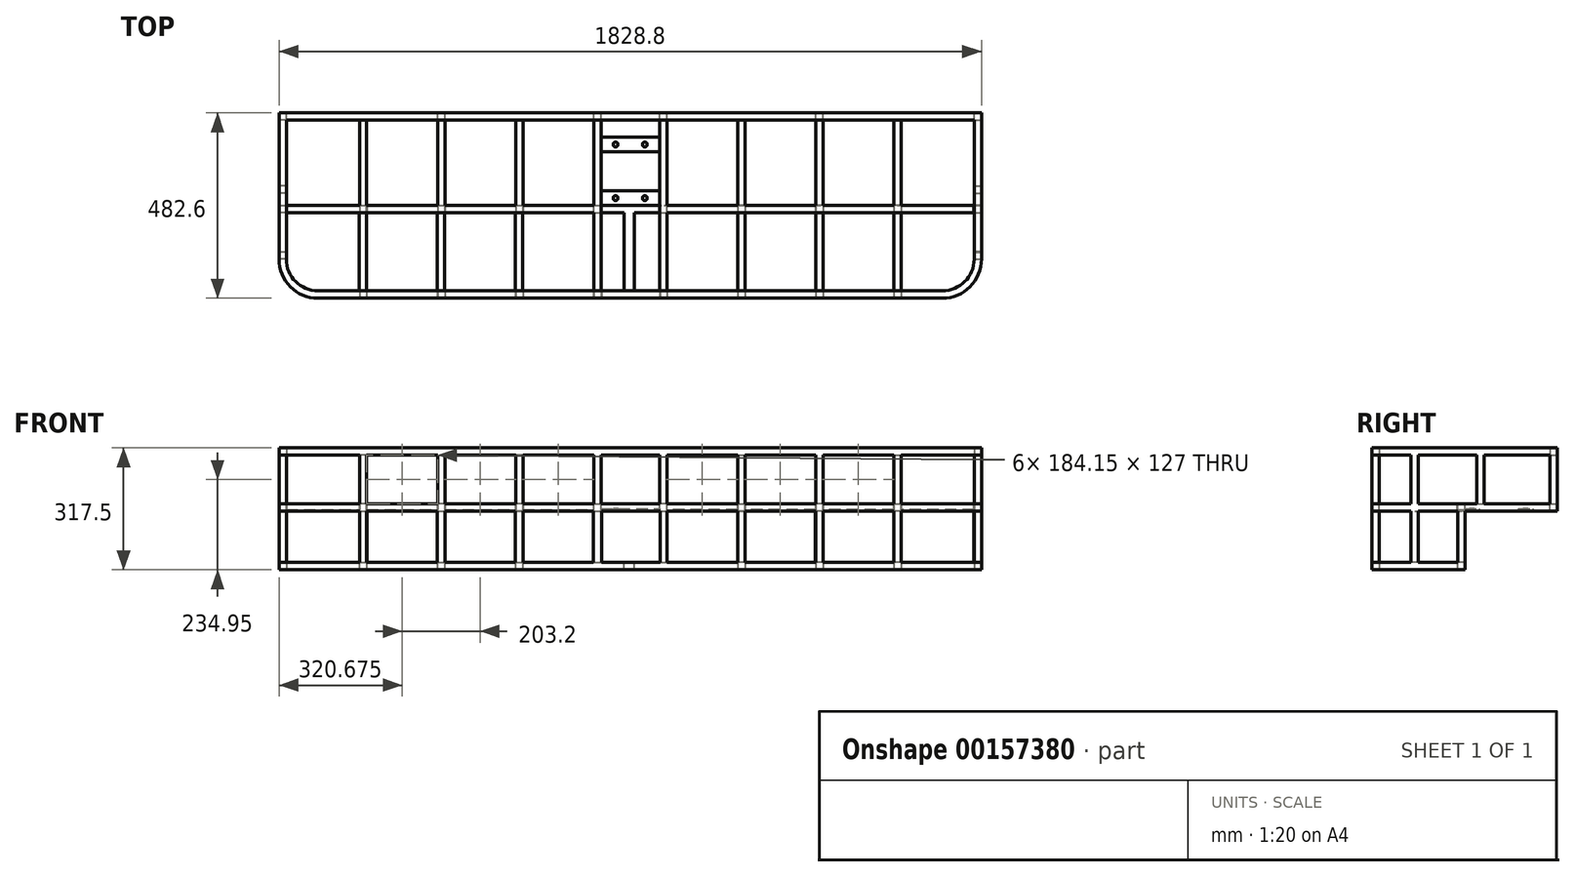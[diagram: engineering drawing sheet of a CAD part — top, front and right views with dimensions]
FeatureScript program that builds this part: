
annotation { "Feature Type Name" : "Feature", "Feature Type Description" : "" }
export const myFeature = defineFeature(function(context is Context, id is Id, definition is map)
    precondition{}
    {
        {
            var Q0;
            Q0=qCreatedBy(makeId("Top.planeOp"),FACE);
            var sketch = newSketch(context, id + "F0", { "sketchPlane" : qUnion([Q0])});
            skLineSegment(sketch, "E0", {"start": v(0, 0) * mm, "end": v(0, -133.91) * mm, "construction": true});
            skLineSegment(sketch, "E1", {"start": v(0, 0) * mm, "end": v(-895.35, 0) * mm});
            skLineSegment(sketch, "E2", {"start": v(-914.4, 0) * mm, "end": v(-914.4, -381) * mm});
            skLineSegment(sketch, "E3", {"start": v(-812.8, -482.6) * mm, "end": v(0, -482.6) * mm});
            skPoint(sketch, "E4.visualSharp", {"position": v(-914.4, -482.6) * mm});
            skArc(sketch, "E4.filletArc", {"start": v(-914.4, -381) * mm, "mid": v(-884.64, -452.84) * mm, "end": v(-812.8, -482.6) * mm});
            skLineSegment(sketch, "E5.0", {"start": v(-812.8, -463.55) * mm, "end": v(0, -463.55) * mm});
            skArc(sketch, "E5.1", {"start": v(-895.35, -381) * mm, "mid": v(-871.17, -439.37) * mm, "end": v(-812.8, -463.55) * mm});
            skLineSegment(sketch, "E5.2", {"start": v(-895.35, -19.05) * mm, "end": v(-895.35, -381) * mm});
            skLineSegment(sketch, "E5.3", {"start": v(0, -19.05) * mm, "end": v(-895.35, -19.05) * mm});
            skLineSegment(sketch, "E6", {"start": v(-895.35, -19.05) * mm, "end": v(-895.35, 0) * mm});
            skLineSegment(sketch, "E7", {"start": v(-914.4, 0) * mm, "end": v(-895.35, 0) * mm});
            skLineSegment(sketch, "E8", {"start": v(0, 0) * mm, "end": v(0, -19.05) * mm});
            skLineSegment(sketch, "E9", {"start": v(0, -463.55) * mm, "end": v(0, -482.6) * mm});
            skSolve(sketch);
        }
        {
            var Q0;
            Q0 = qSketchRegion(id + "F0", true);
            extrude(context, id + "F1", {"entities" : qUnion([Q0]), "depth" : 19.05 * mm});
        }
        {
            var Q0;
            Q0=makeQuery(id+"F1.opExtrude","CAP_FACE",FACE,{"disambiguationData":[OSD([sQuery(id+"F0.wireOp",EDGE,"E1"),sQuery(id+"F0.wireOp",EDGE,"E2"),sQuery(id+"F0.wireOp",EDGE,"E3"),sQuery(id+"F0.wireOp",EDGE,"E4.filletArc"),sQuery(id+"F0.wireOp",EDGE,"E5.0"),sQuery(id+"F0.wireOp",EDGE,"E5.1"),sQuery(id+"F0.wireOp",EDGE,"E5.2"),sQuery(id+"F0.wireOp",EDGE,"E5.3"),sQuery(id+"F0.wireOp",EDGE,"E7"),sQuery(id+"F0.wireOp",EDGE,"E8"),sQuery(id+"F0.wireOp",EDGE,"E9")])],"isStart":false});
            cPlane(context, id + "F2", {"entities" : qUnion([Q0]), "cplaneType" : CPlaneType.OFFSET, "offset" : 127 * mm, "width" : 152.4 * mm, "height" : 152.4 * mm});
        }
        {
            var Q0;
            Q0=qCreatedBy(id+"F2.planeOp",FACE);
            var sketch = newSketch(context, id + "F3", { "sketchPlane" : qUnion([Q0])});
            skLineSegment(sketch, "E10.0", {"start": v(-812.8, -482.6) * mm, "end": v(0, -482.6) * mm});
            skLineSegment(sketch, "E10.1", {"start": v(-812.8, -463.55) * mm, "end": v(0, -463.55) * mm});
            skLineSegment(sketch, "E10.2", {"start": v(0, -463.55) * mm, "end": v(0, -482.6) * mm});
            skArc(sketch, "E10.3", {"start": v(-895.35, -381) * mm, "mid": v(-871.17, -439.37) * mm, "end": v(-812.8, -463.55) * mm});
            skArc(sketch, "E10.4", {"start": v(-914.4, -381) * mm, "mid": v(-884.64, -452.84) * mm, "end": v(-812.8, -482.6) * mm});
            skLineSegment(sketch, "E10.5", {"start": v(-914.4, 0) * mm, "end": v(-914.4, -381) * mm});
            skLineSegment(sketch, "E10.6", {"start": v(-895.35, -19.05) * mm, "end": v(-895.35, -381) * mm});
            skLineSegment(sketch, "E10.7", {"start": v(0, 0) * mm, "end": v(-914.4, 0) * mm});
            skLineSegment(sketch, "E10.8", {"start": v(0, -19.05) * mm, "end": v(-895.35, -19.05) * mm});
            skLineSegment(sketch, "E10.9", {"start": v(0, 0) * mm, "end": v(0, -19.05) * mm});
            skSolve(sketch);
        }
        {
            var Q0;
            Q0 = qSketchRegion(id + "F3", true);
            extrude(context, id + "F4", {"entities" : qUnion([Q0]), "depth" : 19.05 * mm});
        }
        {
            var Q0;
            Q0=makeQuery(id+"F1.opExtrude","CAP_FACE",FACE,{"disambiguationData":[OSD([sQuery(id+"F0.wireOp",EDGE,"E1"),sQuery(id+"F0.wireOp",EDGE,"E2"),sQuery(id+"F0.wireOp",EDGE,"E3"),sQuery(id+"F0.wireOp",EDGE,"E4.filletArc"),sQuery(id+"F0.wireOp",EDGE,"E5.0"),sQuery(id+"F0.wireOp",EDGE,"E5.1"),sQuery(id+"F0.wireOp",EDGE,"E5.2"),sQuery(id+"F0.wireOp",EDGE,"E5.3"),sQuery(id+"F0.wireOp",EDGE,"E7"),sQuery(id+"F0.wireOp",EDGE,"E8"),sQuery(id+"F0.wireOp",EDGE,"E9")])],"isStart":true});
            cPlane(context, id + "F5", {"entities" : qUnion([Q0]), "cplaneType" : CPlaneType.OFFSET, "offset" : 152.4 * mm, "width" : 152.4 * mm, "height" : 152.4 * mm});
        }
        {
            var Q0;
            Q0=qCreatedBy(id+"F5.planeOp",FACE);
            var sketch = newSketch(context, id + "F6", { "sketchPlane" : qUnion([Q0])});
            skLineSegment(sketch, "E11.0", {"start": v(-812.8, 482.6) * mm, "end": v(0, 482.6) * mm});
            skLineSegment(sketch, "E11.1", {"start": v(-812.8, 463.55) * mm, "end": v(0, 463.55) * mm});
            skLineSegment(sketch, "E11.2", {"start": v(0, 463.55) * mm, "end": v(0, 482.6) * mm});
            skArc(sketch, "E11.3", {"start": v(-914.4, 381) * mm, "mid": v(-884.64, 452.84) * mm, "end": v(-812.8, 482.6) * mm});
            skArc(sketch, "E11.4", {"start": v(-895.35, 381) * mm, "mid": v(-871.17, 439.37) * mm, "end": v(-812.8, 463.55) * mm});
            skLineSegment(sketch, "E12", {"start": v(-914.4, 381) * mm, "end": v(-914.4, 240.55) * mm});
            skLineSegment(sketch, "E13", {"start": v(-914.4, 240.55) * mm, "end": v(0, 240.55) * mm});
            skLineSegment(sketch, "E14.0", {"start": v(-895.35, 259.6) * mm, "end": v(0, 259.6) * mm});
            skLineSegment(sketch, "E14.1", {"start": v(-895.35, 381) * mm, "end": v(-895.35, 259.6) * mm});
            skLineSegment(sketch, "E15", {"start": v(0, 259.6) * mm, "end": v(0, 240.55) * mm});
            skSolve(sketch);
        }
        {
            var Q0;
            Q0 = qSketchRegion(id + "F6", true);
            extrude(context, id + "F7", {"entities" : qUnion([Q0]), "oppositeDirection" : true, "depth" : 19.05 * mm});
        }
        {
            var Q0;
            Q0=makeQuery(id+"F1.opExtrude","CAP_FACE",FACE,{"disambiguationData":[OSD([sQuery(id+"F0.wireOp",EDGE,"E1"),sQuery(id+"F0.wireOp",EDGE,"E2"),sQuery(id+"F0.wireOp",EDGE,"E3"),sQuery(id+"F0.wireOp",EDGE,"E4.filletArc"),sQuery(id+"F0.wireOp",EDGE,"E5.0"),sQuery(id+"F0.wireOp",EDGE,"E5.1"),sQuery(id+"F0.wireOp",EDGE,"E5.2"),sQuery(id+"F0.wireOp",EDGE,"E5.3"),sQuery(id+"F0.wireOp",EDGE,"E7"),sQuery(id+"F0.wireOp",EDGE,"E8"),sQuery(id+"F0.wireOp",EDGE,"E9")])],"isStart":false});
            var sketch = newSketch(context, id + "F8", { "sketchPlane" : qUnion([Q0])});
            skLineSegment(sketch, "E16.bottom", {"start": v(-76.2, -463.55) * mm, "end": v(-95.25, -463.55) * mm});
            skLineSegment(sketch, "E16.top", {"start": v(-76.2, -19.05) * mm, "end": v(-95.25, -19.05) * mm});
            skLineSegment(sketch, "E16.left", {"start": v(-76.2, -463.55) * mm, "end": v(-76.2, -19.05) * mm});
            skLineSegment(sketch, "E16.right", {"start": v(-95.25, -463.55) * mm, "end": v(-95.25, -19.05) * mm});
            skLineSegment(sketch, "E17.1.0.0", {"start": v(-279.4, -260.58) * mm, "end": v(-279.4, -19.05) * mm});
            skLineSegment(sketch, "E17.1.0.1", {"start": v(-298.45, -260.58) * mm, "end": v(-298.45, -19.05) * mm});
            skLineSegment(sketch, "E17.1.0.3", {"start": v(-279.4, -19.05) * mm, "end": v(-298.45, -19.05) * mm});
            skLineSegment(sketch, "E17.2.0.0", {"start": v(-482.6, -259.76) * mm, "end": v(-482.6, -19.05) * mm});
            skLineSegment(sketch, "E17.2.0.1", {"start": v(-501.65, -259.76) * mm, "end": v(-501.65, -19.05) * mm});
            skLineSegment(sketch, "E17.2.0.3", {"start": v(-482.6, -19.05) * mm, "end": v(-501.65, -19.05) * mm});
            skLineSegment(sketch, "E17.3.0.0", {"start": v(-685.8, -259.76) * mm, "end": v(-685.8, -19.05) * mm});
            skLineSegment(sketch, "E17.3.0.1", {"start": v(-704.85, -259.76) * mm, "end": v(-704.85, -19.05) * mm});
            skLineSegment(sketch, "E17.3.0.3", {"start": v(-685.8, -19.05) * mm, "end": v(-704.85, -19.05) * mm});
            skLineSegment(sketch, "E17.direction1", {"start": v(-95.25, -463.55) * mm, "end": v(-298.45, -463.55) * mm, "construction": true});
            skLineSegment(sketch, "E18", {"start": v(-482.6, -259.76) * mm, "end": v(-501.65, -259.76) * mm});
            skLineSegment(sketch, "E19.trimOffspring", {"start": v(-685.8, -259.76) * mm, "end": v(-704.85, -259.76) * mm});
            skLineSegment(sketch, "E20", {"start": v(-279.4, -260.58) * mm, "end": v(-298.45, -260.58) * mm});
            skSolve(sketch);
        }
        {
            var Q0;
            Q0 = qSketchRegion(id + "F8", true);
            extrude(context, id + "F9", {"entities" : qUnion([Q0]), "operationType" : NewBodyOperationType.ADD, "oppositeDirection" : true, "depth" : 19.05 * mm});
        }
        {
            var Q0;
            Q0=makeQuery(id+"F9.boolean.opBoolean","MERGE",FACE,{"derivedFrom":[makeQuery(id+"F1.opExtrude","CAP_FACE",FACE,{"disambiguationData":[OSD([sQuery(id+"F0.wireOp",EDGE,"E1"),sQuery(id+"F0.wireOp",EDGE,"E2"),sQuery(id+"F0.wireOp",EDGE,"E3"),sQuery(id+"F0.wireOp",EDGE,"E4.filletArc"),sQuery(id+"F0.wireOp",EDGE,"E5.0"),sQuery(id+"F0.wireOp",EDGE,"E5.1"),sQuery(id+"F0.wireOp",EDGE,"E5.2"),sQuery(id+"F0.wireOp",EDGE,"E5.3"),sQuery(id+"F0.wireOp",EDGE,"E7"),sQuery(id+"F0.wireOp",EDGE,"E8"),sQuery(id+"F0.wireOp",EDGE,"E9")])],"isStart":false}),makeQuery(id+"F9.opExtrude","CAP_FACE",FACE,{"disambiguationData":[OSD([sQuery(id+"F8.wireOp",EDGE,"E16.bottom"),sQuery(id+"F8.wireOp",EDGE,"E16.top"),sQuery(id+"F8.wireOp",EDGE,"E16.left"),sQuery(id+"F8.wireOp",EDGE,"E16.right")])],"isStart":true}),makeQuery(id+"F9.opExtrude","CAP_FACE",FACE,{"disambiguationData":[OSD([sQuery(id+"F8.wireOp",EDGE,"E17.1.0.0"),sQuery(id+"F8.wireOp",EDGE,"E17.1.0.1"),sQuery(id+"F8.wireOp",EDGE,"E17.1.0.2"),sQuery(id+"F8.wireOp",EDGE,"E17.1.0.3")])],"isStart":true}),makeQuery(id+"F9.opExtrude","CAP_FACE",FACE,{"disambiguationData":[OSD([sQuery(id+"F8.wireOp",EDGE,"E17.2.0.0"),sQuery(id+"F8.wireOp",EDGE,"E17.2.0.1"),sQuery(id+"F8.wireOp",EDGE,"E17.2.0.2"),sQuery(id+"F8.wireOp",EDGE,"E17.2.0.3")])],"isStart":true}),makeQuery(id+"F9.opExtrude","CAP_FACE",FACE,{"disambiguationData":[OSD([sQuery(id+"F8.wireOp",EDGE,"E17.3.0.0"),sQuery(id+"F8.wireOp",EDGE,"E17.3.0.1"),sQuery(id+"F8.wireOp",EDGE,"E17.3.0.2"),sQuery(id+"F8.wireOp",EDGE,"E17.3.0.3")])],"isStart":true})]});
            var sketch = newSketch(context, id + "F10", { "sketchPlane" : qUnion([Q0])});
            skLineSegment(sketch, "E21.bottom", {"start": v(-895.35, -19.05) * mm, "end": v(-914.4, -19.05) * mm});
            skLineSegment(sketch, "E21.top", {"start": v(-895.35, 0) * mm, "end": v(-914.4, 0) * mm});
            skLineSegment(sketch, "E21.left", {"start": v(-895.35, -19.05) * mm, "end": v(-895.35, 0) * mm});
            skLineSegment(sketch, "E21.right", {"start": v(-914.4, -19.05) * mm, "end": v(-914.4, 0) * mm});
            skLineSegment(sketch, "E22", {"start": v(-895.35, -200.03) * mm, "end": v(-914.4, -200.03) * mm, "construction": true});
            skLineSegment(sketch, "E23.bottom", {"start": v(-895.35, -209.55) * mm, "end": v(-914.4, -209.55) * mm});
            skLineSegment(sketch, "E23.top", {"start": v(-895.35, -190.5) * mm, "end": v(-914.4, -190.5) * mm});
            skLineSegment(sketch, "E23.left", {"start": v(-895.35, -209.55) * mm, "end": v(-895.35, -190.5) * mm});
            skLineSegment(sketch, "E23.right", {"start": v(-914.4, -209.55) * mm, "end": v(-914.4, -190.5) * mm});
            skPoint(sketch, "E23.middle", {"position": v(-904.88, -200.03) * mm});
            skLineSegment(sketch, "E24.bottom", {"start": v(-914.4, -381) * mm, "end": v(-895.35, -381) * mm});
            skLineSegment(sketch, "E24.top", {"start": v(-914.4, -361.95) * mm, "end": v(-895.35, -361.95) * mm});
            skLineSegment(sketch, "E24.left", {"start": v(-914.4, -381) * mm, "end": v(-914.4, -361.95) * mm});
            skLineSegment(sketch, "E24.right", {"start": v(-895.35, -381) * mm, "end": v(-895.35, -361.95) * mm});
            skLineSegment(sketch, "E25.bottom", {"start": v(-501.65, -19.05) * mm, "end": v(-482.6, -19.05) * mm});
            skLineSegment(sketch, "E25.top", {"start": v(-501.65, 0) * mm, "end": v(-482.6, 0) * mm});
            skLineSegment(sketch, "E25.left", {"start": v(-501.65, -19.05) * mm, "end": v(-501.65, 0) * mm});
            skLineSegment(sketch, "E25.right", {"start": v(-482.6, -19.05) * mm, "end": v(-482.6, 0) * mm});
            skLineSegment(sketch, "E26.bottom", {"start": v(-95.25, -19.05) * mm, "end": v(-76.2, -19.05) * mm});
            skLineSegment(sketch, "E26.top", {"start": v(-95.25, 0) * mm, "end": v(-76.2, 0) * mm});
            skLineSegment(sketch, "E26.left", {"start": v(-95.25, -19.05) * mm, "end": v(-95.25, 0) * mm});
            skLineSegment(sketch, "E26.right", {"start": v(-76.2, -19.05) * mm, "end": v(-76.2, 0) * mm});
            skLineSegment(sketch, "E27.bottom", {"start": v(-704.85, -463.55) * mm, "end": v(-685.8, -463.55) * mm});
            skLineSegment(sketch, "E27.top", {"start": v(-704.85, -482.6) * mm, "end": v(-685.8, -482.6) * mm});
            skLineSegment(sketch, "E27.left", {"start": v(-704.85, -463.55) * mm, "end": v(-704.85, -482.6) * mm});
            skLineSegment(sketch, "E27.right", {"start": v(-685.8, -463.55) * mm, "end": v(-685.8, -482.6) * mm});
            skLineSegment(sketch, "E28.1.0.0", {"start": v(-501.65, -463.55) * mm, "end": v(-501.65, -482.6) * mm});
            skLineSegment(sketch, "E28.1.0.1", {"start": v(-501.65, -463.55) * mm, "end": v(-482.6, -463.55) * mm});
            skLineSegment(sketch, "E28.1.0.2", {"start": v(-482.6, -463.55) * mm, "end": v(-482.6, -482.6) * mm});
            skLineSegment(sketch, "E28.1.0.3", {"start": v(-501.65, -482.6) * mm, "end": v(-482.6, -482.6) * mm});
            skLineSegment(sketch, "E28.2.0.0", {"start": v(-298.45, -463.55) * mm, "end": v(-298.45, -482.6) * mm});
            skLineSegment(sketch, "E28.2.0.1", {"start": v(-298.45, -463.55) * mm, "end": v(-279.4, -463.55) * mm});
            skLineSegment(sketch, "E28.2.0.2", {"start": v(-279.4, -463.55) * mm, "end": v(-279.4, -482.6) * mm});
            skLineSegment(sketch, "E28.2.0.3", {"start": v(-298.45, -482.6) * mm, "end": v(-279.4, -482.6) * mm});
            skLineSegment(sketch, "E28.3.0.0", {"start": v(-95.25, -463.55) * mm, "end": v(-95.25, -482.6) * mm});
            skLineSegment(sketch, "E28.3.0.1", {"start": v(-95.25, -463.55) * mm, "end": v(-76.2, -463.55) * mm});
            skLineSegment(sketch, "E28.3.0.2", {"start": v(-76.2, -463.55) * mm, "end": v(-76.2, -482.6) * mm});
            skLineSegment(sketch, "E28.3.0.3", {"start": v(-95.25, -482.6) * mm, "end": v(-76.2, -482.6) * mm});
            skLineSegment(sketch, "E28.direction1", {"start": v(-704.85, -482.6) * mm, "end": v(-501.65, -482.6) * mm, "construction": true});
            skSolve(sketch);
        }
        {
            var Q0;
            Q0 = qSketchRegion(id + "F10", true);
            extrude(context, id + "F11", {"entities" : qUnion([Q0]), "operationType" : NewBodyOperationType.ADD, "endBound" : BoundingType.UP_TO_NEXT, "depth" : 25.4 * mm});
        }
        {
            var Q0;
            Q0=makeQuery(id+"FObIPIXqjTfMBa8_3.boolean.opBoolean","MERGE",FACE,{"derivedFrom":[makeQuery(id+"F7.opExtrude","CAP_FACE",FACE,{"disambiguationData":[OSD([sQuery(id+"F6.wireOp",EDGE,"E11.0"),sQuery(id+"F6.wireOp",EDGE,"E11.1"),sQuery(id+"F6.wireOp",EDGE,"E11.2"),sQuery(id+"F6.wireOp",EDGE,"E11.3"),sQuery(id+"F6.wireOp",EDGE,"E11.4"),sQuery(id+"F6.wireOp",EDGE,"E12"),sQuery(id+"F6.wireOp",EDGE,"E13"),sQuery(id+"F6.wireOp",EDGE,"E14.0"),sQuery(id+"F6.wireOp",EDGE,"E14.1"),sQuery(id+"F6.wireOp",EDGE,"E15")])],"isStart":false}),makeQuery(id+"FObIPIXqjTfMBa8_3.opExtrude","CAP_FACE",FACE,{"disambiguationData":[OSD([sQuery(id+"F0IQqYHni9HqBG3_3.wireOp",EDGE,"jzNje37I-5EXG-MEss-oUQA-cgiQJYgBRHcg.bottom"),sQuery(id+"F0IQqYHni9HqBG3_3.wireOp",EDGE,"jzNje37I-5EXG-MEss-oUQA-cgiQJYgBRHcg.top"),sQuery(id+"F0IQqYHni9HqBG3_3.wireOp",EDGE,"572f668a-fa3e-4ea4-a201-f8e6f7c56c95.0"),sQuery(id+"F0IQqYHni9HqBG3_3.wireOp",EDGE,"572f668a-fa3e-4ea4-a201-f8e6f7c56c95.1")])],"isStart":false}),makeQuery(id+"FObIPIXqjTfMBa8_3.opExtrude","CAP_FACE",FACE,{"disambiguationData":[OSD([sQuery(id+"F0IQqYHni9HqBG3_3.wireOp",EDGE,"65659cea-a670-4d87-9673-9ee32ba60e3a.1.0.0"),sQuery(id+"F0IQqYHni9HqBG3_3.wireOp",EDGE,"65659cea-a670-4d87-9673-9ee32ba60e3a.1.0.1"),sQuery(id+"F0IQqYHni9HqBG3_3.wireOp",EDGE,"65659cea-a670-4d87-9673-9ee32ba60e3a.1.0.2"),sQuery(id+"F0IQqYHni9HqBG3_3.wireOp",EDGE,"65659cea-a670-4d87-9673-9ee32ba60e3a.1.0.3")])],"isStart":false}),makeQuery(id+"FObIPIXqjTfMBa8_3.opExtrude","CAP_FACE",FACE,{"disambiguationData":[OSD([sQuery(id+"F0IQqYHni9HqBG3_3.wireOp",EDGE,"65659cea-a670-4d87-9673-9ee32ba60e3a.2.0.0"),sQuery(id+"F0IQqYHni9HqBG3_3.wireOp",EDGE,"65659cea-a670-4d87-9673-9ee32ba60e3a.2.0.1"),sQuery(id+"F0IQqYHni9HqBG3_3.wireOp",EDGE,"65659cea-a670-4d87-9673-9ee32ba60e3a.2.0.2"),sQuery(id+"F0IQqYHni9HqBG3_3.wireOp",EDGE,"65659cea-a670-4d87-9673-9ee32ba60e3a.2.0.3")])],"isStart":false})]});
            var sketch = newSketch(context, id + "F12", { "sketchPlane" : qUnion([Q0])});
            skLineSegment(sketch, "E29.bottom", {"start": v(-895.27, -240.55) * mm, "end": v(-914.4, -240.55) * mm});
            skLineSegment(sketch, "E29.top", {"start": v(-895.27, -259.68) * mm, "end": v(-914.4, -259.68) * mm});
            skLineSegment(sketch, "E29.left", {"start": v(-895.27, -240.55) * mm, "end": v(-895.27, -259.68) * mm});
            skLineSegment(sketch, "E29.right", {"start": v(-914.4, -240.55) * mm, "end": v(-914.4, -259.68) * mm});
            skLineSegment(sketch, "E30.bottom", {"start": v(-685.8, -463.55) * mm, "end": v(-704.85, -463.55) * mm});
            skLineSegment(sketch, "E30.top", {"start": v(-685.8, -482.6) * mm, "end": v(-704.85, -482.6) * mm});
            skLineSegment(sketch, "E30.left", {"start": v(-685.8, -463.55) * mm, "end": v(-685.8, -482.6) * mm});
            skLineSegment(sketch, "E30.right", {"start": v(-704.85, -463.55) * mm, "end": v(-704.85, -482.6) * mm});
            skLineSegment(sketch, "E31.bottom", {"start": v(-482.6, -463.55) * mm, "end": v(-501.71, -463.55) * mm});
            skLineSegment(sketch, "E31.top", {"start": v(-482.6, -482.6) * mm, "end": v(-501.71, -482.6) * mm});
            skLineSegment(sketch, "E31.left", {"start": v(-482.6, -463.55) * mm, "end": v(-482.6, -482.6) * mm});
            skLineSegment(sketch, "E31.right", {"start": v(-501.71, -463.55) * mm, "end": v(-501.71, -482.6) * mm});
            skLineSegment(sketch, "E32.bottom", {"start": v(-279.4, -463.55) * mm, "end": v(-298.9, -463.55) * mm});
            skLineSegment(sketch, "E32.top", {"start": v(-279.4, -482.6) * mm, "end": v(-298.9, -482.6) * mm});
            skLineSegment(sketch, "E32.left", {"start": v(-279.4, -463.55) * mm, "end": v(-279.4, -482.6) * mm});
            skLineSegment(sketch, "E32.right", {"start": v(-298.9, -463.55) * mm, "end": v(-298.9, -482.6) * mm});
            skLineSegment(sketch, "E33.bottom", {"start": v(-685.77, -240.55) * mm, "end": v(-704.85, -240.55) * mm});
            skLineSegment(sketch, "E33.top", {"start": v(-685.77, -259.6) * mm, "end": v(-704.85, -259.6) * mm});
            skLineSegment(sketch, "E33.left", {"start": v(-685.77, -240.55) * mm, "end": v(-685.77, -259.6) * mm});
            skLineSegment(sketch, "E33.right", {"start": v(-704.85, -240.55) * mm, "end": v(-704.85, -259.6) * mm});
            skLineSegment(sketch, "E34.bottom", {"start": v(-482.34, -240.55) * mm, "end": v(-501.65, -240.55) * mm});
            skLineSegment(sketch, "E34.top", {"start": v(-482.34, -259.6) * mm, "end": v(-501.65, -259.6) * mm});
            skLineSegment(sketch, "E34.left", {"start": v(-482.34, -240.55) * mm, "end": v(-482.34, -259.6) * mm});
            skLineSegment(sketch, "E34.right", {"start": v(-501.65, -240.55) * mm, "end": v(-501.65, -259.6) * mm});
            skLineSegment(sketch, "E35.bottom", {"start": v(-279.5, -240.55) * mm, "end": v(-298.45, -240.55) * mm});
            skLineSegment(sketch, "E35.top", {"start": v(-279.5, -259.6) * mm, "end": v(-298.45, -259.6) * mm});
            skLineSegment(sketch, "E35.left", {"start": v(-279.5, -240.55) * mm, "end": v(-279.5, -259.6) * mm});
            skLineSegment(sketch, "E35.right", {"start": v(-298.45, -240.55) * mm, "end": v(-298.45, -259.6) * mm});
            skLineSegment(sketch, "E36.bottom", {"start": v(-895.35, -381) * mm, "end": v(-914.4, -381) * mm});
            skLineSegment(sketch, "E36.top", {"start": v(-895.35, -362.5) * mm, "end": v(-914.4, -362.5) * mm});
            skLineSegment(sketch, "E36.left", {"start": v(-895.35, -381) * mm, "end": v(-895.35, -362.5) * mm});
            skLineSegment(sketch, "E36.right", {"start": v(-914.4, -381) * mm, "end": v(-914.4, -362.5) * mm});
            skSolve(sketch);
        }
        {
            var Q0;
            Q0 = qSketchRegion(id + "F12", true);
            var Q1;
            Q1=makeQuery(id+"F9.boolean.opBoolean","MERGE",FACE,{"derivedFrom":[makeQuery(id+"F1.opExtrude","CAP_FACE",FACE,{"disambiguationData":[OSD([sQuery(id+"F0.wireOp",EDGE,"E1"),sQuery(id+"F0.wireOp",EDGE,"E2"),sQuery(id+"F0.wireOp",EDGE,"E3"),sQuery(id+"F0.wireOp",EDGE,"E4.filletArc"),sQuery(id+"F0.wireOp",EDGE,"E5.0"),sQuery(id+"F0.wireOp",EDGE,"E5.1"),sQuery(id+"F0.wireOp",EDGE,"E5.2"),sQuery(id+"F0.wireOp",EDGE,"E5.3"),sQuery(id+"F0.wireOp",EDGE,"E7"),sQuery(id+"F0.wireOp",EDGE,"E8"),sQuery(id+"F0.wireOp",EDGE,"E9")])],"isStart":true}),makeQuery(id+"F9.opExtrude","CAP_FACE",FACE,{"disambiguationData":[OSD([sQuery(id+"F8.wireOp",EDGE,"E16.bottom"),sQuery(id+"F8.wireOp",EDGE,"E16.top"),sQuery(id+"F8.wireOp",EDGE,"E16.left"),sQuery(id+"F8.wireOp",EDGE,"E16.right")])],"isStart":false}),makeQuery(id+"F9.opExtrude","CAP_FACE",FACE,{"disambiguationData":[OSD([sQuery(id+"F8.wireOp",EDGE,"E17.1.0.0"),sQuery(id+"F8.wireOp",EDGE,"E17.1.0.1"),sQuery(id+"F8.wireOp",EDGE,"E17.1.0.2"),sQuery(id+"F8.wireOp",EDGE,"E17.1.0.3")])],"isStart":false}),makeQuery(id+"F9.opExtrude","CAP_FACE",FACE,{"disambiguationData":[OSD([sQuery(id+"F8.wireOp",EDGE,"E17.2.0.0"),sQuery(id+"F8.wireOp",EDGE,"E17.2.0.1"),sQuery(id+"F8.wireOp",EDGE,"E17.2.0.2"),sQuery(id+"F8.wireOp",EDGE,"E17.2.0.3")])],"isStart":false}),makeQuery(id+"F9.opExtrude","CAP_FACE",FACE,{"disambiguationData":[OSD([sQuery(id+"F8.wireOp",EDGE,"E17.3.0.0"),sQuery(id+"F8.wireOp",EDGE,"E17.3.0.1"),sQuery(id+"F8.wireOp",EDGE,"E17.3.0.2"),sQuery(id+"F8.wireOp",EDGE,"E17.3.0.3")])],"isStart":false})]});
            extrude(context, id + "F13", {"entities" : qUnion([Q0]), "operationType" : NewBodyOperationType.ADD, "endBound" : BoundingType.UP_TO_SURFACE, "endBoundEntityFace" : qUnion([Q1]), "depth" : 25.4 * mm});
        }
        {
            var Q0;
            {var subQ0=makeQuery(id+"F9.opExtrude","CAP_FACE",FACE,{"disambiguationData":[OSD([sQuery(id+"F8.wireOp",EDGE,"E17.2.0.0"),sQuery(id+"F8.wireOp",EDGE,"E17.2.0.1"),sQuery(id+"F8.wireOp",EDGE,"E17.2.0.3"),sQuery(id+"F8.wireOp",EDGE,"E18")])],"isStart":true});var subQ1=makeQuery(id+"F9.opExtrude","CAP_FACE",FACE,{"disambiguationData":[OSD([sQuery(id+"F8.wireOp",EDGE,"E17.1.0.0"),sQuery(id+"F8.wireOp",EDGE,"E17.1.0.1"),sQuery(id+"F8.wireOp",EDGE,"E17.1.0.3"),sQuery(id+"F8.wireOp",EDGE,"E20")])],"isStart":true});var subQ2=sQuery(id+"F8.wireOp",EDGE,"E16.left");var subQ3=sQuery(id+"F8.wireOp",EDGE,"E16.right");var subQ4=makeQuery(id+"F9.opExtrude","CAP_FACE",FACE,{"disambiguationData":[OSD([sQuery(id+"F8.wireOp",EDGE,"E16.bottom"),sQuery(id+"F8.wireOp",EDGE,"E16.top"),subQ2,subQ3])],"isStart":true});var subQ5=sQuery(id+"F0.wireOp",EDGE,"E5.3");var subQ6=sQuery(id+"F0.wireOp",EDGE,"E5.0");var subQ7=makeQuery(id+"F1.opExtrude","CAP_FACE",FACE,{"disambiguationData":[OSD([sQuery(id+"F0.wireOp",EDGE,"E1"),sQuery(id+"F0.wireOp",EDGE,"E2"),sQuery(id+"F0.wireOp",EDGE,"E3"),sQuery(id+"F0.wireOp",EDGE,"E4.filletArc"),subQ6,sQuery(id+"F0.wireOp",EDGE,"E5.1"),sQuery(id+"F0.wireOp",EDGE,"E5.2"),subQ5,sQuery(id+"F0.wireOp",EDGE,"E7"),sQuery(id+"F0.wireOp",EDGE,"E8"),sQuery(id+"F0.wireOp",EDGE,"E9")])],"isStart":false});var subQ8=makeQuery(id+"F9.opExtrude","CAP_FACE",FACE,{"disambiguationData":[OSD([sQuery(id+"F8.wireOp",EDGE,"E17.3.0.0"),sQuery(id+"F8.wireOp",EDGE,"E17.3.0.1"),sQuery(id+"F8.wireOp",EDGE,"E17.3.0.3"),sQuery(id+"F8.wireOp",EDGE,"E19.trimOffspring")])],"isStart":true});Q0=makeQuery(id+"F11.boolean.opBoolean","SPLIT",FACE,{"disambiguationData":[TD([subQ7,makeQuery(id+"F1.opExtrude","SWEPT_FACE",FACE,{"disambiguationData":[OSD([subQ6])]}),makeQuery(id+"F1.opExtrude","SWEPT_FACE",FACE,{"disambiguationData":[OSD([subQ5])]}),makeQuery(id+"F4.opExtrude","SWEPT_FACE",FACE,{"disambiguationData":[OSD([sQuery(id+"F3.wireOp",EDGE,"E10.1")])]}),makeQuery(id+"F4.opExtrude","SWEPT_FACE",FACE,{"disambiguationData":[OSD([sQuery(id+"F3.wireOp",EDGE,"E10.8")])]}),subQ4,makeQuery(id+"F9.opExtrude","SWEPT_FACE",FACE,{"disambiguationData":[OSD([subQ2])]}),makeQuery(id+"F9.opExtrude","SWEPT_FACE",FACE,{"disambiguationData":[OSD([subQ3])]}),subQ1,subQ0,subQ8,makeQuery(id+"F11.opExtrude","SWEPT_FACE",FACE,{"disambiguationData":[OSD([sQuery(id+"F10.wireOp",EDGE,"E25.bottom")])]}),makeQuery(id+"F11.opExtrude","SWEPT_FACE",FACE,{"disambiguationData":[OSD([sQuery(id+"F10.wireOp",EDGE,"E26.bottom")])]}),makeQuery(id+"F11.opExtrude","SWEPT_FACE",FACE,{"disambiguationData":[OSD([sQuery(id+"F10.wireOp",EDGE,"E26.left")])]}),makeQuery(id+"F11.opExtrude","SWEPT_FACE",FACE,{"disambiguationData":[OSD([sQuery(id+"F10.wireOp",EDGE,"E26.right")])]}),makeQuery(id+"F11.opExtrude","SWEPT_FACE",FACE,{"disambiguationData":[OSD([sQuery(id+"F10.wireOp",EDGE,"E27.bottom")])]}),makeQuery(id+"F11.opExtrude","SWEPT_FACE",FACE,{"disambiguationData":[OSD([sQuery(id+"F10.wireOp",EDGE,"E28.1.0.1")])]}),makeQuery(id+"F11.opExtrude","SWEPT_FACE",FACE,{"disambiguationData":[OSD([sQuery(id+"F10.wireOp",EDGE,"E28.2.0.1")])]}),makeQuery(id+"F11.opExtrude","SWEPT_FACE",FACE,{"disambiguationData":[OSD([sQuery(id+"F10.wireOp",EDGE,"E28.3.0.0")])]}),makeQuery(id+"F11.opExtrude","SWEPT_FACE",FACE,{"disambiguationData":[OSD([sQuery(id+"F10.wireOp",EDGE,"E28.3.0.1")])]}),makeQuery(id+"F11.opExtrude","SWEPT_FACE",FACE,{"disambiguationData":[OSD([sQuery(id+"F10.wireOp",EDGE,"E28.3.0.2")])]})])],"derivedFrom":makeQuery(id+"F9.boolean.opBoolean","MERGE",FACE,{"derivedFrom":[subQ7,subQ4,subQ1,subQ0,subQ8]})});}
            var sketch = newSketch(context, id + "F14", { "sketchPlane" : qUnion([Q0])});
            skLineSegment(sketch, "E37.0", {"start": v(-895.27, -259.6) * mm, "end": v(-704.85, -259.6) * mm, "construction": true});
            skLineSegment(sketch, "E37.1", {"start": v(-895.27, -240.55) * mm, "end": v(-704.85, -240.55) * mm, "construction": true});
            skPoint(sketch, "E38.oppositeSnap0", {"position": v(-800.06, -240.55) * mm});
            skLineSegment(sketch, "E38.bottom", {"start": v(-895.27, -259.6) * mm, "end": v(-95.25, -259.6) * mm});
            skLineSegment(sketch, "E38.top", {"start": v(-895.27, -240.55) * mm, "end": v(-95.25, -240.55) * mm});
            skLineSegment(sketch, "E38.left", {"start": v(-895.27, -259.6) * mm, "end": v(-895.27, -240.55) * mm});
            skLineSegment(sketch, "E38.right", {"start": v(-95.25, -259.6) * mm, "end": v(-95.25, -240.55) * mm});
            skSolve(sketch);
        }
        {
            var Q0;
            Q0=makeQuery(id+"F14.imprint","IMPRINT",FACE,{"disambiguationData":[TD([[makeQuery(id+"F14.imprint","IMPRINT",EDGE,{"derivedFrom":sQuery(id+"F14.wireOp",EDGE,"E38.bottom")}),1.0]])]});
            extrude(context, id + "F15", {"entities" : qUnion([Q0]), "operationType" : NewBodyOperationType.ADD, "oppositeDirection" : true, "depth" : 15.24 * mm});
        }
        {
            var Q0;
            Q0=makeQuery(id+"F7.opExtrude","CAP_FACE",FACE,{"disambiguationData":[OSD([sQuery(id+"F6.wireOp",EDGE,"E11.0"),sQuery(id+"F6.wireOp",EDGE,"E11.1"),sQuery(id+"F6.wireOp",EDGE,"E11.2"),sQuery(id+"F6.wireOp",EDGE,"E11.3"),sQuery(id+"F6.wireOp",EDGE,"E11.4"),sQuery(id+"F6.wireOp",EDGE,"E12"),sQuery(id+"F6.wireOp",EDGE,"E13"),sQuery(id+"F6.wireOp",EDGE,"E14.0"),sQuery(id+"F6.wireOp",EDGE,"E14.1"),sQuery(id+"F6.wireOp",EDGE,"E15")])],"isStart":true});
            var sketch = newSketch(context, id + "F16", { "sketchPlane" : qUnion([Q0])});
            skLineSegment(sketch, "E39.bottom", {"start": v(-705.4, 259.6) * mm, "end": v(-686.43, 259.6) * mm});
            skLineSegment(sketch, "E39.top", {"start": v(-705.4, 463.55) * mm, "end": v(-686.43, 463.55) * mm});
            skLineSegment(sketch, "E39.left", {"start": v(-705.4, 259.6) * mm, "end": v(-705.4, 463.55) * mm});
            skLineSegment(sketch, "E39.right", {"start": v(-686.43, 259.6) * mm, "end": v(-686.43, 463.55) * mm});
            skLineSegment(sketch, "E40.1.0.0", {"start": v(-483.23, 259.6) * mm, "end": v(-483.23, 463.55) * mm});
            skLineSegment(sketch, "E40.1.0.1", {"start": v(-502.2, 259.6) * mm, "end": v(-502.2, 463.55) * mm});
            skLineSegment(sketch, "E40.1.0.2", {"start": v(-502.2, 463.55) * mm, "end": v(-483.23, 463.55) * mm});
            skLineSegment(sketch, "E40.1.0.3", {"start": v(-502.2, 259.6) * mm, "end": v(-483.23, 259.6) * mm});
            skLineSegment(sketch, "E40.2.0.0", {"start": v(-280.03, 259.6) * mm, "end": v(-280.03, 463.55) * mm});
            skLineSegment(sketch, "E40.2.0.1", {"start": v(-299, 259.6) * mm, "end": v(-299, 463.55) * mm});
            skLineSegment(sketch, "E40.2.0.2", {"start": v(-299, 463.55) * mm, "end": v(-280.03, 463.55) * mm});
            skLineSegment(sketch, "E40.2.0.3", {"start": v(-299, 259.6) * mm, "end": v(-280.03, 259.6) * mm});
            skLineSegment(sketch, "E40.direction1", {"start": v(-705.4, 259.6) * mm, "end": v(-502.2, 259.6) * mm, "construction": true});
            skSolve(sketch);
        }
        {
            var Q0;
            Q0 = qSketchRegion(id + "F16", true);
            extrude(context, id + "F17", {"entities" : qUnion([Q0]), "operationType" : NewBodyOperationType.ADD, "oppositeDirection" : true, "depth" : 19.05 * mm});
        }
        {
            var Q0;
            {var subQ1=sQuery(id+"F8.wireOp",EDGE,"E20");var subQ2=sQuery(id+"F8.wireOp",EDGE,"E16.right");var subQ3=sQuery(id+"F0.wireOp",EDGE,"E3");var subQ4=sQuery(id+"F8.wireOp",EDGE,"E17.1.0.1");var subQ5=sQuery(id+"F8.wireOp",EDGE,"E17.3.0.1");var subQ6=sQuery(id+"F8.wireOp",EDGE,"E17.1.0.0");var subQ8=sQuery(id+"F8.wireOp",EDGE,"E17.3.0.0");var subQ9=sQuery(id+"F8.wireOp",EDGE,"E17.2.0.1");var subQ10=sQuery(id+"F0.wireOp",EDGE,"E5.3");var subQ11=sQuery(id+"F0.wireOp",EDGE,"E9");var subQ12=sQuery(id+"F0.wireOp",EDGE,"E5.2");var subQ13=sQuery(id+"F0.wireOp",EDGE,"E8");var subQ14=sQuery(id+"F0.wireOp",EDGE,"E2");var subQ15=sQuery(id+"F0.wireOp",EDGE,"E5.0");var subQ16=sQuery(id+"F8.wireOp",EDGE,"E17.2.0.0");var subQ17=sQuery(id+"F8.wireOp",EDGE,"E16.left");var subQ19=sQuery(id+"F0.wireOp",EDGE,"E7");var subQ20=sQuery(id+"F0.wireOp",EDGE,"E1");var subQ26=sQuery(id+"F8.wireOp",EDGE,"E19.trimOffspring");var subQ27=sQuery(id+"F8.wireOp",EDGE,"E18");var subQ28=sQuery(id+"F8.wireOp",EDGE,"E17.3.0.3");var subQ29=sQuery(id+"F8.wireOp",EDGE,"E17.2.0.3");var subQ30=sQuery(id+"F8.wireOp",EDGE,"E17.1.0.3");var subQ31=sQuery(id+"F8.wireOp",EDGE,"E16.top");var subQ32=sQuery(id+"F8.wireOp",EDGE,"E16.bottom");var subQ33=sQuery(id+"F0.wireOp",EDGE,"E5.1");var subQ34=sQuery(id+"F0.wireOp",EDGE,"E4.filletArc");Q0=makeQuery(id+"F13.boolean.opBoolean","SPLIT",FACE,{"disambiguationData":[TD([makeQuery(id+"F1.opExtrude","SWEPT_FACE",FACE,{"disambiguationData":[OSD([subQ10])]})])],"derivedFrom":makeQuery(id+"F9.boolean.opBoolean","MERGE",FACE,{"derivedFrom":[makeQuery(id+"F1.opExtrude","CAP_FACE",FACE,{"disambiguationData":[OSD([subQ20,subQ14,subQ3,subQ34,subQ15,subQ33,subQ12,subQ10,subQ19,subQ13,subQ11])],"isStart":true}),makeQuery(id+"F9.opExtrude","CAP_FACE",FACE,{"disambiguationData":[OSD([subQ32,subQ31,subQ17,subQ2])],"isStart":false}),makeQuery(id+"F9.opExtrude","CAP_FACE",FACE,{"disambiguationData":[OSD([subQ6,subQ4,subQ30,subQ1])],"isStart":false}),makeQuery(id+"F9.opExtrude","CAP_FACE",FACE,{"disambiguationData":[OSD([subQ16,subQ9,subQ29,subQ27])],"isStart":false}),makeQuery(id+"F9.opExtrude","CAP_FACE",FACE,{"disambiguationData":[OSD([subQ8,subQ5,subQ28,subQ26])],"isStart":false})]})});}
            var sketch = newSketch(context, id + "F18", { "sketchPlane" : qUnion([Q0])});
            skLineSegment(sketch, "E41.bottom", {"start": v(-76.2, 63.5) * mm, "end": v(0, 63.5) * mm});
            skLineSegment(sketch, "E41.top", {"start": v(-76.2, 101.6) * mm, "end": v(0, 101.6) * mm});
            skLineSegment(sketch, "E41.left", {"start": v(-76.2, 63.5) * mm, "end": v(-76.2, 101.6) * mm});
            skLineSegment(sketch, "E41.right", {"start": v(0, 63.5) * mm, "end": v(0, 101.6) * mm});
            skPoint(sketch, "E42.oppositeSnap0", {"position": v(-76.2, 241.3) * mm});
            skLineSegment(sketch, "E42.bottom", {"start": v(-76.2, 203.2) * mm, "end": v(0, 203.2) * mm});
            skLineSegment(sketch, "E42.top", {"start": v(-76.2, 241.3) * mm, "end": v(0, 241.3) * mm});
            skLineSegment(sketch, "E42.left", {"start": v(-76.2, 203.2) * mm, "end": v(-76.2, 241.3) * mm});
            skLineSegment(sketch, "E42.right", {"start": v(0, 203.2) * mm, "end": v(0, 241.3) * mm});
            skSolve(sketch);
        }
        {
            var Q0;
            Q0 = qSketchRegion(id + "F18", true);
            extrude(context, id + "F19", {"entities" : qUnion([Q0]), "operationType" : NewBodyOperationType.ADD, "oppositeDirection" : true, "depth" : 6.35 * mm});
        }
        {
            var Q0;
            Q0=makeQuery(id+"F19.opExtrude","CAP_FACE",FACE,{"disambiguationData":[OSD([sQuery(id+"F18.wireOp",EDGE,"E41.bottom"),sQuery(id+"F18.wireOp",EDGE,"E41.top"),sQuery(id+"F18.wireOp",EDGE,"E41.left"),sQuery(id+"F18.wireOp",EDGE,"E41.right")])],"isStart":false});
            var sketch = newSketch(context, id + "F20", { "sketchPlane" : qUnion([Q0])});
            skLineSegment(sketch, "E43.0", {"start": v(-76.2, -203.2) * mm, "end": v(0, -203.2) * mm, "construction": true});
            skLineSegment(sketch, "E44.0", {"start": v(-76.2, -241.3) * mm, "end": v(0, -241.3) * mm, "construction": true});
            skLineSegment(sketch, "E45", {"start": v(-38.1, -203.2) * mm, "end": v(-38.1, -241.3) * mm, "construction": true});
            skCircle(sketch, "E46", {"center": v(-38.1, -222.25) * mm, "radius": 6.35 * mm});
            skLineSegment(sketch, "E47", {"start": v(-76.2, -82.55) * mm, "end": v(0, -82.55) * mm, "construction": true});
            skCircle(sketch, "E48", {"center": v(-38.1, -82.55) * mm, "radius": 6.35 * mm});
            skSolve(sketch);
        }
        {
            var Q0;
            Q0 = qSketchRegion(id + "F20", true);
            extrude(context, id + "F21", {"entities" : qUnion([Q0]), "operationType" : NewBodyOperationType.REMOVE, "oppositeDirection" : true, "depth" : 10.16 * mm});
        }
        {
            var Q0;
            Q0=makeQuery(id+"F4.opExtrude","SWEPT_FACE",FACE,{"disambiguationData":[OSD([sQuery(id+"F3.wireOp",EDGE,"E10.2")])]});
            cPlane(context, id + "F22", {"entities" : qUnion([Q0]), "cplaneType" : CPlaneType.OFFSET, "offset" : 0 * mm, "width" : 152.4 * mm, "height" : 152.4 * mm});
        }
        {
            var Q0;
            Q0=makeQuery(id+"F1.opExtrude","SWEPT_BODY",BODY,{"disambiguationData":[OSD([sQuery(id+"F0.wireOp",EDGE,"E1"),sQuery(id+"F0.wireOp",EDGE,"E2"),sQuery(id+"F0.wireOp",EDGE,"E3"),sQuery(id+"F0.wireOp",EDGE,"E4.filletArc"),sQuery(id+"F0.wireOp",EDGE,"E5.0"),sQuery(id+"F0.wireOp",EDGE,"E5.1"),sQuery(id+"F0.wireOp",EDGE,"E5.2"),sQuery(id+"F0.wireOp",EDGE,"E5.3"),sQuery(id+"F0.wireOp",EDGE,"E7"),sQuery(id+"F0.wireOp",EDGE,"E8"),sQuery(id+"F0.wireOp",EDGE,"E9")])]});
            var Q1;
            Q1=qCreatedBy(id+"F22.planeOp",FACE);
            mirror(context, id + "F23", {"operationType" : NewBodyOperationType.ADD, "entities" : qUnion([Q0]), "mirrorPlane" : qUnion([Q1])});
        }
        {
            var Q0;
            {var subQ0=makeQuery(id+"F13.boolean.opBoolean","MERGE",FACE,{"derivedFrom":[makeQuery(id+"F7.opExtrude","SWEPT_FACE",FACE,{"disambiguationData":[OSD([sQuery(id+"F6.wireOp",EDGE,"E11.0")])]}),makeQuery(id+"F11.boolean.opBoolean","MERGE",FACE,{"derivedFrom":[makeQuery(id+"F1.opExtrude","SWEPT_FACE",FACE,{"disambiguationData":[OSD([sQuery(id+"F0.wireOp",EDGE,"E3")])]}),makeQuery(id+"F4.opExtrude","SWEPT_FACE",FACE,{"disambiguationData":[OSD([sQuery(id+"F3.wireOp",EDGE,"E10.0")])]}),makeQuery(id+"F11.opExtrude","SWEPT_FACE",FACE,{"disambiguationData":[OSD([sQuery(id+"F10.wireOp",EDGE,"E27.top")])]}),makeQuery(id+"F11.opExtrude","SWEPT_FACE",FACE,{"disambiguationData":[OSD([sQuery(id+"F10.wireOp",EDGE,"E28.1.0.3")])]}),makeQuery(id+"F11.opExtrude","SWEPT_FACE",FACE,{"disambiguationData":[OSD([sQuery(id+"F10.wireOp",EDGE,"E28.2.0.3")])]}),makeQuery(id+"F11.opExtrude","SWEPT_FACE",FACE,{"disambiguationData":[OSD([sQuery(id+"F10.wireOp",EDGE,"E28.3.0.3")])]})]}),makeQuery(id+"F13.opExtrude","SWEPT_FACE",FACE,{"disambiguationData":[OSD([sQuery(id+"F12.wireOp",EDGE,"E30.top")])]}),makeQuery(id+"F13.opExtrude","SWEPT_FACE",FACE,{"disambiguationData":[OSD([sQuery(id+"F12.wireOp",EDGE,"E31.top")])]}),makeQuery(id+"F13.opExtrude","SWEPT_FACE",FACE,{"disambiguationData":[OSD([sQuery(id+"F12.wireOp",EDGE,"E32.top")])]})]});Q0=makeQuery(id+"F23.boolean.opBoolean","MERGE",FACE,{"derivedFrom":[subQ0,makeQuery(id+"F23.opPattern","COPY",FACE,{"derivedFrom":subQ0,"instanceName":"1"})]});}
            var sketch = newSketch(context, id + "F24", { "sketchPlane" : qUnion([Q0])});
            skLineSegment(sketch, "E49.bottom", {"start": v(-96.25, 0) * mm, "end": v(-74.49, 0) * mm});
            skLineSegment(sketch, "E49.top", {"start": v(-96.25, -133.35) * mm, "end": v(-74.49, -133.35) * mm});
            skLineSegment(sketch, "E49.left", {"start": v(-96.25, 0) * mm, "end": v(-96.25, -133.35) * mm});
            skLineSegment(sketch, "E49.right", {"start": v(-74.49, 0) * mm, "end": v(-74.49, -133.35) * mm});
            skLineSegment(sketch, "E50.bottom", {"start": v(78.44, 0) * mm, "end": v(96.3, 0) * mm});
            skLineSegment(sketch, "E50.top", {"start": v(78.44, -133.35) * mm, "end": v(96.3, -133.35) * mm});
            skLineSegment(sketch, "E50.left", {"start": v(78.44, 0) * mm, "end": v(78.44, -133.35) * mm});
            skLineSegment(sketch, "E50.right", {"start": v(96.3, 0) * mm, "end": v(96.3, -133.35) * mm});
            skSolve(sketch);
        }
        {
            var Q0;
            Q0 = qSketchRegion(id + "F24", true);
            extrude(context, id + "F25", {"entities" : qUnion([Q0]), "operationType" : NewBodyOperationType.ADD, "oppositeDirection" : true, "depth" : 19.05 * mm});
        }
        {
            var Q0;
            {var subQ0=makeQuery(id+"F17.boolean.opBoolean","MERGE",FACE,{"derivedFrom":[makeQuery(id+"F7.opExtrude","CAP_FACE",FACE,{"disambiguationData":[OSD([sQuery(id+"F6.wireOp",EDGE,"E11.0"),sQuery(id+"F6.wireOp",EDGE,"E11.1"),sQuery(id+"F6.wireOp",EDGE,"E11.2"),sQuery(id+"F6.wireOp",EDGE,"E11.3"),sQuery(id+"F6.wireOp",EDGE,"E11.4"),sQuery(id+"F6.wireOp",EDGE,"E12"),sQuery(id+"F6.wireOp",EDGE,"E13"),sQuery(id+"F6.wireOp",EDGE,"E14.0"),sQuery(id+"F6.wireOp",EDGE,"E14.1"),sQuery(id+"F6.wireOp",EDGE,"E15")])],"isStart":true}),makeQuery(id+"F17.opExtrude","CAP_FACE",FACE,{"disambiguationData":[OSD([sQuery(id+"F16.wireOp",EDGE,"E39.bottom"),sQuery(id+"F16.wireOp",EDGE,"E39.top"),sQuery(id+"F16.wireOp",EDGE,"E39.left"),sQuery(id+"F16.wireOp",EDGE,"E39.right")])],"isStart":true}),makeQuery(id+"F17.opExtrude","CAP_FACE",FACE,{"disambiguationData":[OSD([sQuery(id+"F16.wireOp",EDGE,"E40.1.0.0"),sQuery(id+"F16.wireOp",EDGE,"E40.1.0.1"),sQuery(id+"F16.wireOp",EDGE,"E40.1.0.2"),sQuery(id+"F16.wireOp",EDGE,"E40.1.0.3")])],"isStart":true}),makeQuery(id+"F17.opExtrude","CAP_FACE",FACE,{"disambiguationData":[OSD([sQuery(id+"F16.wireOp",EDGE,"E40.2.0.0"),sQuery(id+"F16.wireOp",EDGE,"E40.2.0.1"),sQuery(id+"F16.wireOp",EDGE,"E40.2.0.2"),sQuery(id+"F16.wireOp",EDGE,"E40.2.0.3")])],"isStart":true})]});Q0=makeQuery(id+"F23.boolean.opBoolean","MERGE",FACE,{"derivedFrom":[subQ0,makeQuery(id+"F23.opPattern","COPY",FACE,{"derivedFrom":subQ0,"instanceName":"1"})]});}
            var sketch = newSketch(context, id + "F26", { "sketchPlane" : qUnion([Q0])});
            skLineSegment(sketch, "E51.bottom", {"start": v(-16.08, 482.6) * mm, "end": v(10.76, 482.6) * mm});
            skLineSegment(sketch, "E51.top", {"start": v(-16.08, 240.55) * mm, "end": v(10.76, 240.55) * mm});
            skLineSegment(sketch, "E51.left", {"start": v(-16.08, 482.6) * mm, "end": v(-16.08, 240.55) * mm});
            skLineSegment(sketch, "E51.right", {"start": v(10.76, 482.6) * mm, "end": v(10.76, 240.55) * mm});
            skSolve(sketch);
        }
        {
            var Q0;
            Q0 = qSketchRegion(id + "F26", true);
            extrude(context, id + "F27", {"entities" : qUnion([Q0]), "operationType" : NewBodyOperationType.ADD, "oppositeDirection" : true, "depth" : 19.05 * mm});
        }
    });
